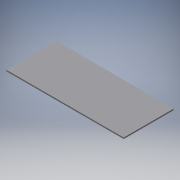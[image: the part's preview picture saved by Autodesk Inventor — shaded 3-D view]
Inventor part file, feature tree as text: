
AUTODESK INVENTOR PART (.ipt)
format: ipt  version: 2018.2 (Build 222227000, 227)  size: 90,624 bytes
history: native  units: in
note: dims shown in document units (in); Inventor stores cm internally (conversion verified against a paired STEP export)
features: extrude x1, sketch x1
ambient origin geometry x8: Origin, YZ Plane, XZ Plane, XY Plane, X Axis, Y Axis, Z Axis, Center Point
bodies: Solid1 (feature_tree)
feature tree (2):
  extrude  "Extrusion1"  Depth=0.75in
  sketch  "Sketch1"  dims[d0=65.727in d1=0.75in d2=28.226in d3=0.0in]
